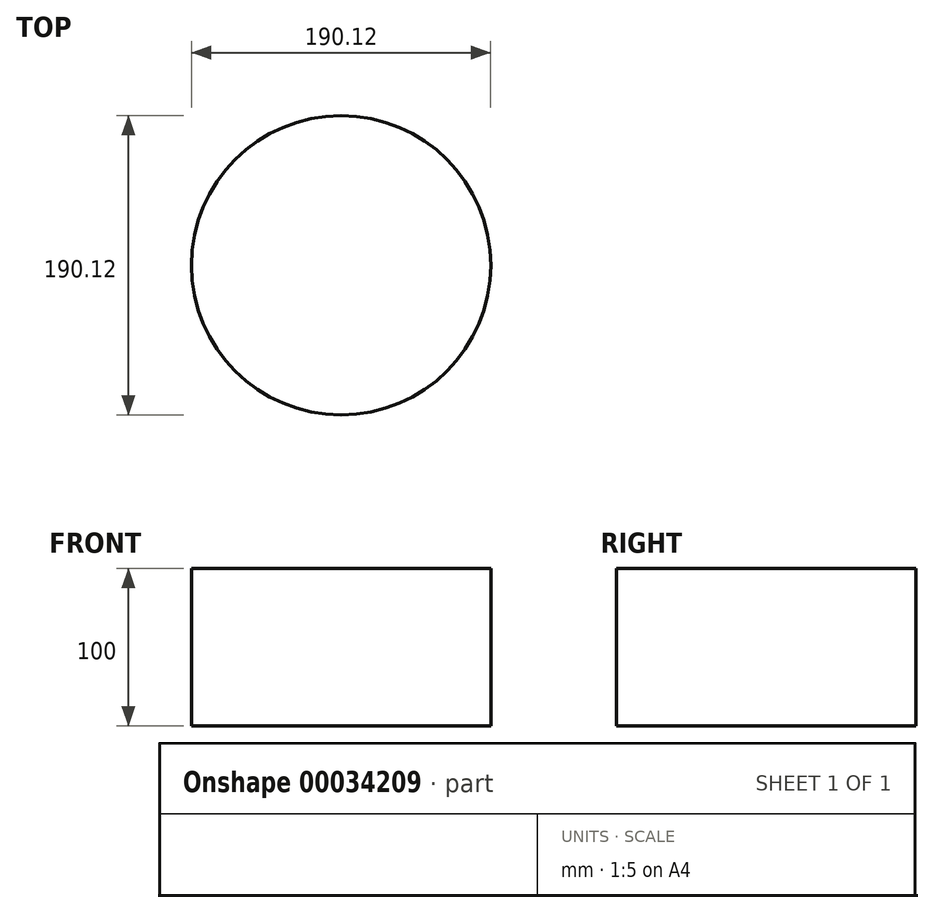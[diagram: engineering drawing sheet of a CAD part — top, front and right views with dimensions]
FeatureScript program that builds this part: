
annotation { "Feature Type Name" : "Feature", "Feature Type Description" : "" }
export const myFeature = defineFeature(function(context is Context, id is Id, definition is map)
    precondition{}
    {
        {
            var Q0;
            Q0=qCreatedBy(makeId("Top.planeOp"),FACE);
            var sketch = newSketch(context, id + "F0", { "sketchPlane" : qUnion([Q0])});
            skCircle(sketch, "E0", {"center": v(0, 0) * mm, "radius": 95.06 * mm});
            skSolve(sketch);
        }
        {
            var Q0;
            Q0=makeQuery(id+"F0.imprint","IMPRINT",FACE,{"disambiguationData":[TD([[makeQuery(id+"F0.imprint","IMPRINT",EDGE,{"derivedFrom":sQuery(id+"F0.wireOp",EDGE,"E0")}),1.0]])]});
            var Q1;
            Q1=sQuery(id+"F0.wireOp",EDGE,"E0");
            extrude(context, id + "F1", {"entities" : qUnion([Q0]), "bodyType" : ExtendedToolBodyType.SURFACE, "surfaceEntities" : qUnion([Q1]), "depth" : 100 * mm});
        }
    });
